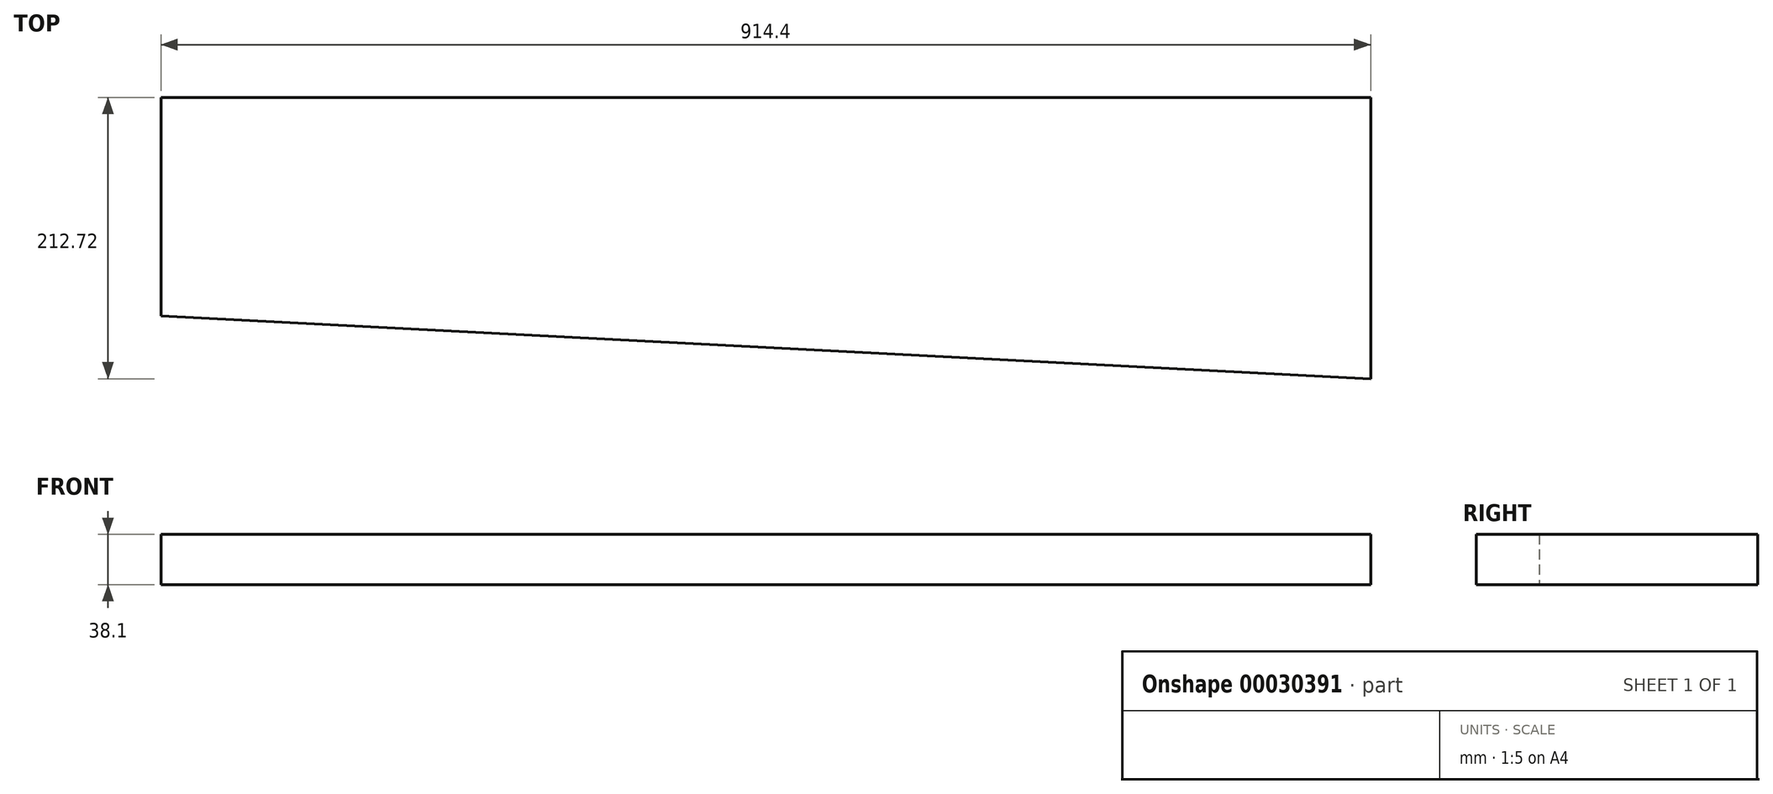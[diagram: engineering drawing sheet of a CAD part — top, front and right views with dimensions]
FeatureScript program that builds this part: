
annotation { "Feature Type Name" : "Feature", "Feature Type Description" : "" }
export const myFeature = defineFeature(function(context is Context, id is Id, definition is map)
    precondition{}
    {
        {
            var Q0;
            Q0=qCreatedBy(makeId("Top.planeOp"),FACE);
            var sketch = newSketch(context, id + "F0", { "sketchPlane" : qUnion([Q0])});
            skLineSegment(sketch, "E0", {"start": v(0, 0) * mm, "end": v(914.4, 0) * mm});
            skLineSegment(sketch, "E1", {"start": v(914.4, 0) * mm, "end": v(914.4, -212.73) * mm});
            skLineSegment(sketch, "E2", {"start": v(914.4, -212.73) * mm, "end": v(0, -165.1) * mm});
            skLineSegment(sketch, "E3", {"start": v(0, -165.1) * mm, "end": v(0, 0) * mm});
            skSolve(sketch);
        }
        {
            var Q0;
            Q0=makeQuery(id+"F0.imprint","IMPRINT",FACE,{"disambiguationData":[TD([[makeQuery(id+"F0.imprint","IMPRINT",EDGE,{"derivedFrom":sQuery(id+"F0.wireOp",EDGE,"E0")}),-1.0]])]});
            extrude(context, id + "F1", {"entities" : qUnion([Q0]), "endBound" : BoundingType.SYMMETRIC, "depth" : 38.1 * mm});
        }
    });
